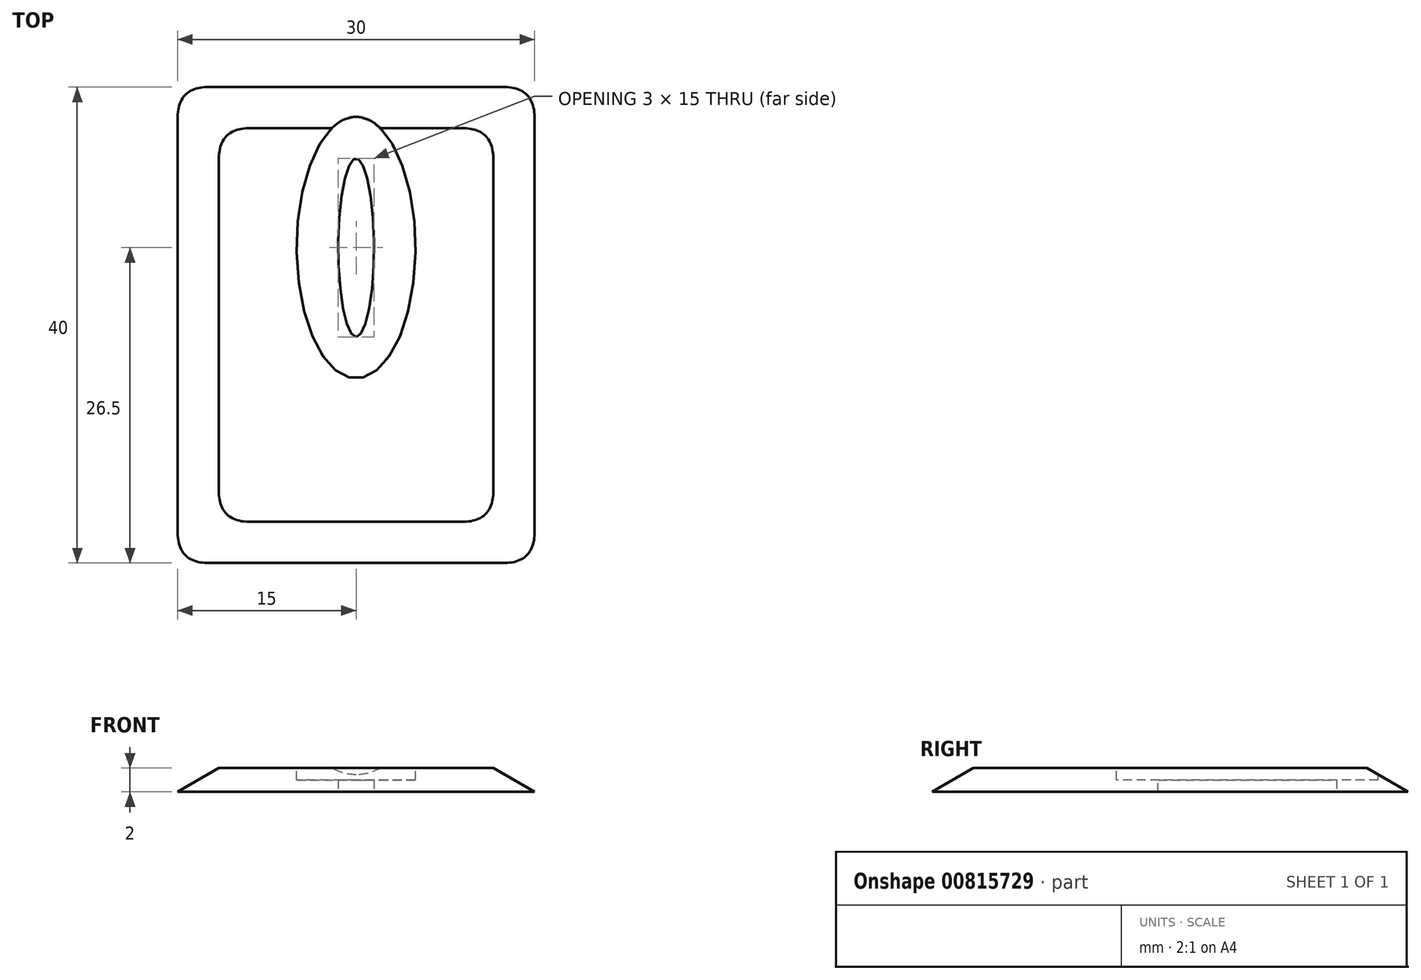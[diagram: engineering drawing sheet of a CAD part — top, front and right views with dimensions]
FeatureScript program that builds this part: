
annotation { "Feature Type Name" : "Feature", "Feature Type Description" : "" }
export const myFeature = defineFeature(function(context is Context, id is Id, definition is map)
    precondition{}
    {
        {
            var Q0;
            Q0=qCreatedBy(makeId("Top.planeOp"),FACE);
            var sketch = newSketch(context, id + "F0", { "sketchPlane" : qUnion([Q0])});
            skLineSegment(sketch, "E0.bottom", {"start": v(0, 0) * mm, "end": v(30, 0) * mm});
            skLineSegment(sketch, "E0.top", {"start": v(0, 40) * mm, "end": v(30, 40) * mm});
            skLineSegment(sketch, "E0.left", {"start": v(0, 0) * mm, "end": v(0, 40) * mm});
            skLineSegment(sketch, "E0.right", {"start": v(30, 0) * mm, "end": v(30, 40) * mm});
            skSolve(sketch);
        }
        {
            var Q0;
            Q0=makeQuery(id+"F0.imprint","IMPRINT",FACE,{"disambiguationData":[TD([[makeQuery(id+"F0.imprint","IMPRINT",EDGE,{"derivedFrom":sQuery(id+"F0.wireOp",EDGE,"E0.bottom")}),1.0]])]});
            extrude(context, id + "F1", {"entities" : qUnion([Q0]), "depth" : 2 * mm, "offsetDistance" : 25 * mm});
        }
        {
            var Q0;
            Q0=makeQuery(id+"F1.opExtrude","CAP_FACE",FACE,{"disambiguationData":[OSD([sQuery(id+"F0.wireOp",EDGE,"E0.bottom"),sQuery(id+"F0.wireOp",EDGE,"E0.top"),sQuery(id+"F0.wireOp",EDGE,"E0.left"),sQuery(id+"F0.wireOp",EDGE,"E0.right")])],"isStart":false});
            var sketch = newSketch(context, id + "F2", { "sketchPlane" : qUnion([Q0])});
            skEllipse(sketch, "E1", {"center": v(15, 26.5) * mm, "majorRadius": 7.5 * mm, "minorRadius": 1.5 * mm, "majorAxis": v(0, -1)});
            skEllipse(sketch, "E2", {"center": v(15, 26.5) * mm, "majorRadius": 11 * mm, "minorRadius": 5 * mm, "majorAxis": v(0, 1)});
            skSolve(sketch);
        }
        {
            var Q0;
            Q0=makeQuery(id+"F2.imprint","IMPRINT",FACE,{"disambiguationData":[TD([[makeQuery(id+"F2.imprint","IMPRINT",EDGE,{"derivedFrom":sQuery(id+"F2.wireOp",EDGE,"E1")}),-1.0]])]});
            extrude(context, id + "F3", {"entities" : qUnion([Q0]), "operationType" : NewBodyOperationType.REMOVE, "oppositeDirection" : true, "depth" : 1 * mm, "offsetDistance" : 25 * mm});
        }
        {
            var Q0;
            Q0=makeQuery(id+"F3.boolean.opBoolean","SPLIT",FACE,{"disambiguationData":[TD([makeQuery(id+"F3.opExtrude","SWEPT_FACE",FACE,{"disambiguationData":[OSD([sQuery(id+"F2.wireOp",EDGE,"E1")])]})])],"derivedFrom":makeQuery(id+"F1.opExtrude","CAP_FACE",FACE,{"disambiguationData":[OSD([sQuery(id+"F0.wireOp",EDGE,"E0.bottom"),sQuery(id+"F0.wireOp",EDGE,"E0.top"),sQuery(id+"F0.wireOp",EDGE,"E0.left"),sQuery(id+"F0.wireOp",EDGE,"E0.right")])],"isStart":false})});
            extrude(context, id + "F4", {"entities" : qUnion([Q0]), "operationType" : NewBodyOperationType.REMOVE, "oppositeDirection" : true, "depth" : 2 * mm, "offsetDistance" : 25 * mm});
        }
        {
            var Q0;
            Q0=makeQuery(id+"F1.opExtrude","CAP_EDGE",EDGE,{"disambiguationData":[OSD([sQuery(id+"F0.wireOp",EDGE,"E0.bottom")])],"isStart":false});
            var Q1;
            Q1=makeQuery(id+"F1.opExtrude","CAP_EDGE",EDGE,{"disambiguationData":[OSD([sQuery(id+"F0.wireOp",EDGE,"E0.right")])],"isStart":false});
            var Q2;
            Q2=makeQuery(id+"F1.opExtrude","CAP_EDGE",EDGE,{"disambiguationData":[OSD([sQuery(id+"F0.wireOp",EDGE,"E0.top")])],"isStart":false});
            var Q3;
            Q3=makeQuery(id+"F1.opExtrude","CAP_EDGE",EDGE,{"disambiguationData":[OSD([sQuery(id+"F0.wireOp",EDGE,"E0.left")])],"isStart":false});
            chamfer(context, id + "F5", {"entities" : qUnion([Q0, Q1, Q2, Q3]), "chamferType" : ChamferType.OFFSET_ANGLE, "width" : 2 * mm, "oppositeDirection" : false, "angle" : 60 * degree, "tangentPropagation" : true});
        }
        {
            var Q0;
            Q0=makeQuery(id+"F5.opChamfer","BLEND_EDGE",EDGE,{"blendedFrom":[makeQuery(id+"F1.opExtrude","CAP_EDGE",EDGE,{"disambiguationData":[OSD([sQuery(id+"F0.wireOp",EDGE,"E0.top")])],"isStart":false}),makeQuery(id+"F1.opExtrude","CAP_EDGE",EDGE,{"disambiguationData":[OSD([sQuery(id+"F0.wireOp",EDGE,"E0.right")])],"isStart":false})],"blendedInto":[]});
            var Q1;
            Q1=makeQuery(id+"F5.opChamfer","BLEND_EDGE",EDGE,{"blendedFrom":[makeQuery(id+"F1.opExtrude","CAP_EDGE",EDGE,{"disambiguationData":[OSD([sQuery(id+"F0.wireOp",EDGE,"E0.bottom")])],"isStart":false}),makeQuery(id+"F1.opExtrude","CAP_EDGE",EDGE,{"disambiguationData":[OSD([sQuery(id+"F0.wireOp",EDGE,"E0.right")])],"isStart":false})],"blendedInto":[]});
            var Q2;
            Q2=makeQuery(id+"F5.opChamfer","BLEND_EDGE",EDGE,{"blendedFrom":[makeQuery(id+"F1.opExtrude","CAP_EDGE",EDGE,{"disambiguationData":[OSD([sQuery(id+"F0.wireOp",EDGE,"E0.bottom")])],"isStart":false}),makeQuery(id+"F1.opExtrude","CAP_EDGE",EDGE,{"disambiguationData":[OSD([sQuery(id+"F0.wireOp",EDGE,"E0.left")])],"isStart":false})],"blendedInto":[]});
            var Q3;
            Q3=makeQuery(id+"F5.opChamfer","BLEND_EDGE",EDGE,{"blendedFrom":[makeQuery(id+"F1.opExtrude","CAP_EDGE",EDGE,{"disambiguationData":[OSD([sQuery(id+"F0.wireOp",EDGE,"E0.top")])],"isStart":false}),makeQuery(id+"F1.opExtrude","CAP_EDGE",EDGE,{"disambiguationData":[OSD([sQuery(id+"F0.wireOp",EDGE,"E0.left")])],"isStart":false})],"blendedInto":[]});
            fillet(context, id + "F6", {"entities" : qUnion([Q0, Q1, Q2, Q3]), "radius" : 5 * mm, "tangentPropagation" : true, "allowEdgeOverflow" : false});
        }
    });
